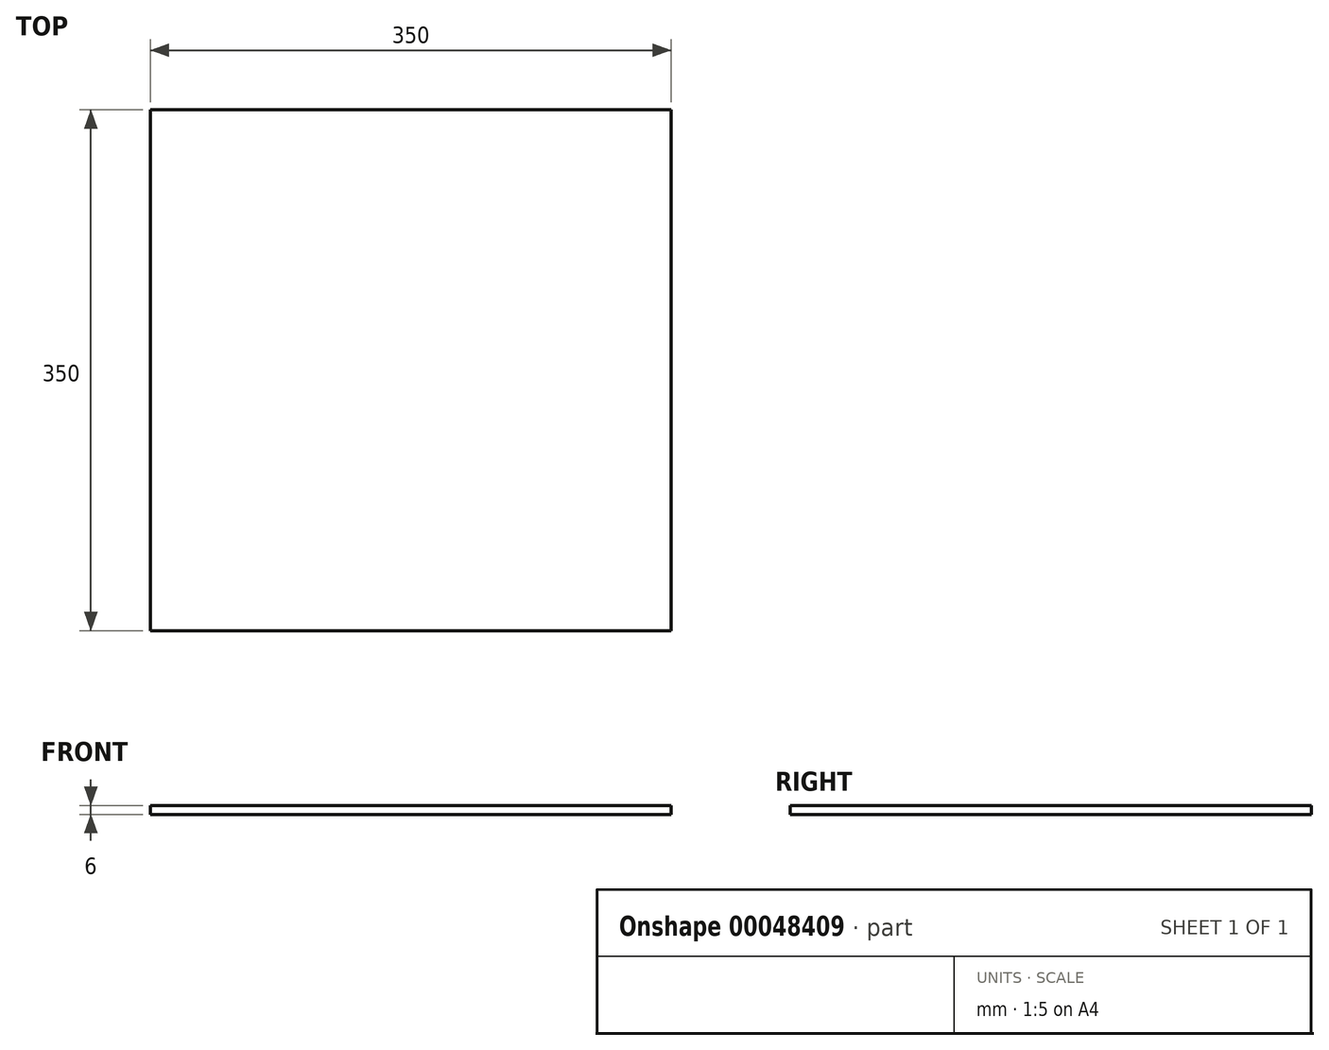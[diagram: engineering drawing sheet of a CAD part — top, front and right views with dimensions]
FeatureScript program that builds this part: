
annotation { "Feature Type Name" : "Feature", "Feature Type Description" : "" }
export const myFeature = defineFeature(function(context is Context, id is Id, definition is map)
    precondition{}
    {
        {
            var Q0;
            Q0=qCreatedBy(makeId("Top.planeOp"),FACE);
            var sketch = newSketch(context, id + "F0", { "sketchPlane" : qUnion([Q0])});
            skLineSegment(sketch, "E0.bottom", {"start": v(0, 0) * mm, "end": v(350, 0) * mm});
            skLineSegment(sketch, "E0.top", {"start": v(0, 350) * mm, "end": v(350, 350) * mm});
            skLineSegment(sketch, "E0.left", {"start": v(0, 0) * mm, "end": v(0, 350) * mm});
            skLineSegment(sketch, "E0.right", {"start": v(350, 0) * mm, "end": v(350, 350) * mm});
            skSolve(sketch);
        }
        {
            var Q0;
            Q0=makeQuery(id+"F0.imprint","IMPRINT",FACE,{"disambiguationData":[TD([[makeQuery(id+"F0.imprint","IMPRINT",EDGE,{"derivedFrom":sQuery(id+"F0.wireOp",EDGE,"E0.bottom")}),1.0]])]});
            extrude(context, id + "F1", {"entities" : qUnion([Q0]), "depth" : 6 * mm});
        }
    });
